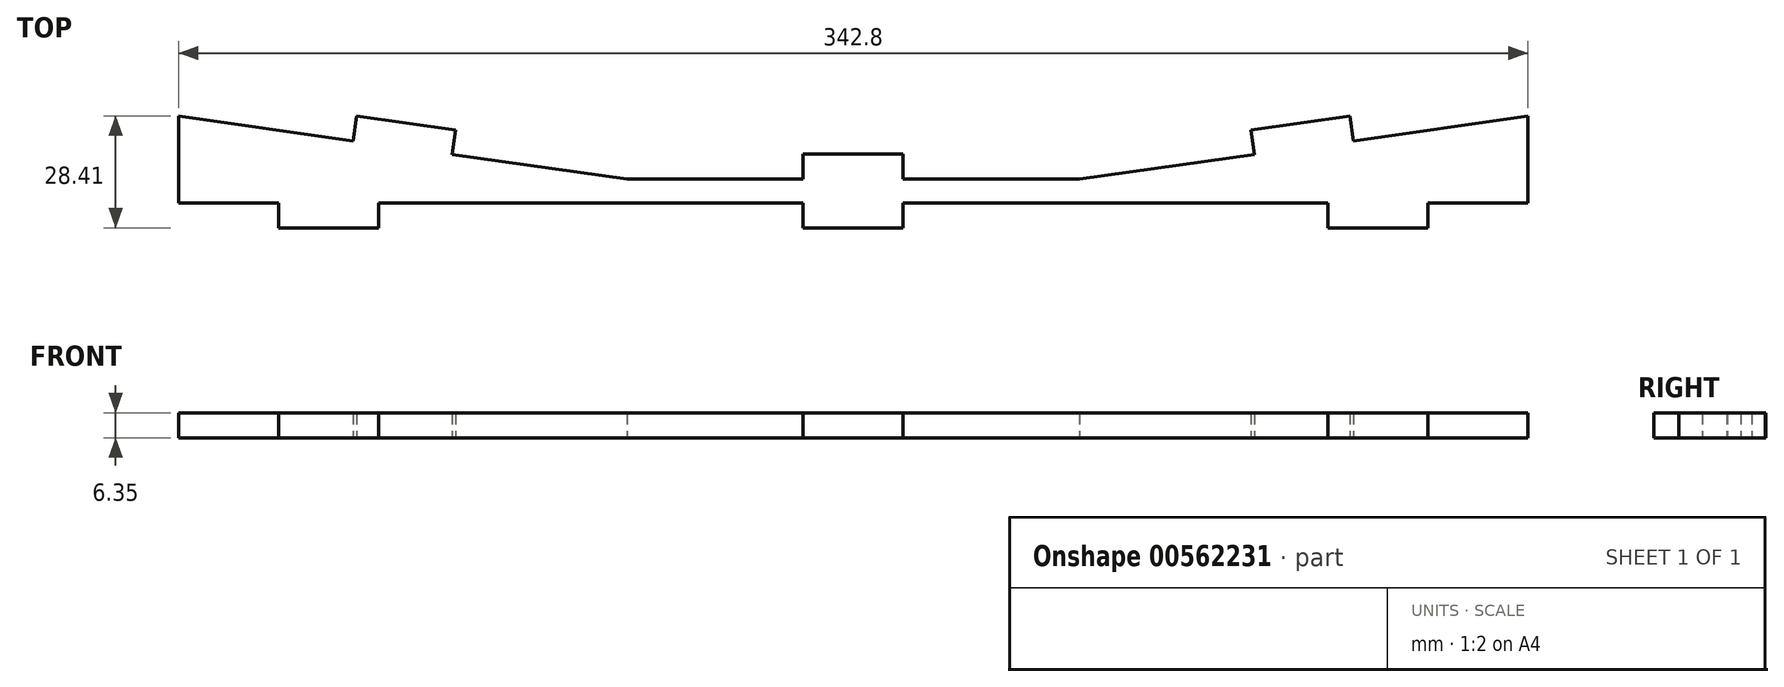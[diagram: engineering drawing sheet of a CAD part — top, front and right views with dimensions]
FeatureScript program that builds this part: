
annotation { "Feature Type Name" : "Feature", "Feature Type Description" : "" }
export const myFeature = defineFeature(function(context is Context, id is Id, definition is map)
    precondition{}
    {
        {
            var Q0;
            Q0=qCreatedBy(makeId("Top.planeOp"),FACE);
            var sketch = newSketch(context, id + "F0", { "sketchPlane" : qUnion([Q0])});
            skLineSegment(sketch, "E0", {"start": v(-171.4, 0) * mm, "end": v(171.4, 0) * mm});
            skLineSegment(sketch, "E1", {"start": v(-171.4, 0) * mm, "end": v(-171.4, 22) * mm});
            skLineSegment(sketch, "E2", {"start": v(-171.4, 22) * mm, "end": v(-57.5, 6) * mm});
            skLineSegment(sketch, "E3", {"start": v(-57.5, 6) * mm, "end": v(57.5, 6) * mm});
            skLineSegment(sketch, "E4", {"start": v(57.5, 6) * mm, "end": v(171.4, 22) * mm});
            skLineSegment(sketch, "E5", {"start": v(171.4, 22) * mm, "end": v(171.4, 0) * mm});
            skPoint(sketch, "E6.orphan", {"position": v(236.34, 0) * mm});
            skLineSegment(sketch, "E7", {"start": v(-146, 0) * mm, "end": v(-146, -6.35) * mm});
            skLineSegment(sketch, "E8", {"start": v(-146, -6.35) * mm, "end": v(-120.6, -6.35) * mm});
            skLineSegment(sketch, "E9", {"start": v(-120.6, -6.35) * mm, "end": v(-120.6, 0) * mm});
            skLineSegment(sketch, "E10", {"start": v(146, 0) * mm, "end": v(146, -6.35) * mm});
            skLineSegment(sketch, "E11", {"start": v(146, -6.35) * mm, "end": v(120.6, -6.35) * mm});
            skLineSegment(sketch, "E12", {"start": v(120.6, -6.35) * mm, "end": v(120.6, 0) * mm});
            skLineSegment(sketch, "E13", {"start": v(-12.7, 0) * mm, "end": v(-12.7, -6.35) * mm});
            skLineSegment(sketch, "E14", {"start": v(-12.7, -6.35) * mm, "end": v(12.7, -6.35) * mm});
            skLineSegment(sketch, "E15", {"start": v(12.7, -6.35) * mm, "end": v(12.7, 0) * mm});
            skLineSegment(sketch, "E16", {"start": v(-127.03, 15.77) * mm, "end": v(-126.15, 22.06) * mm});
            skLineSegment(sketch, "E17", {"start": v(-126.15, 22.06) * mm, "end": v(-101, 18.52) * mm});
            skLineSegment(sketch, "E18", {"start": v(-101, 18.52) * mm, "end": v(-101.88, 12.23) * mm});
            skLineSegment(sketch, "E19", {"start": v(-12.7, 6) * mm, "end": v(-12.7, 12.35) * mm});
            skLineSegment(sketch, "E20", {"start": v(-12.7, 12.35) * mm, "end": v(12.7, 12.35) * mm});
            skLineSegment(sketch, "E21", {"start": v(12.7, 12.35) * mm, "end": v(12.7, 6) * mm});
            skLineSegment(sketch, "E22", {"start": v(101.88, 12.23) * mm, "end": v(101, 18.52) * mm});
            skLineSegment(sketch, "E23", {"start": v(101, 18.52) * mm, "end": v(126.15, 22.06) * mm});
            skLineSegment(sketch, "E24", {"start": v(126.15, 22.06) * mm, "end": v(127.03, 15.77) * mm});
            skSolve(sketch);
        }
        {
            var Q0;
            Q0 = qSketchRegion(id + "F0", true);
            extrude(context, id + "F1", {"entities" : qUnion([Q0]), "depth" : 6.35 * mm, "offsetDistance" : 25.4 * mm});
        }
    });
